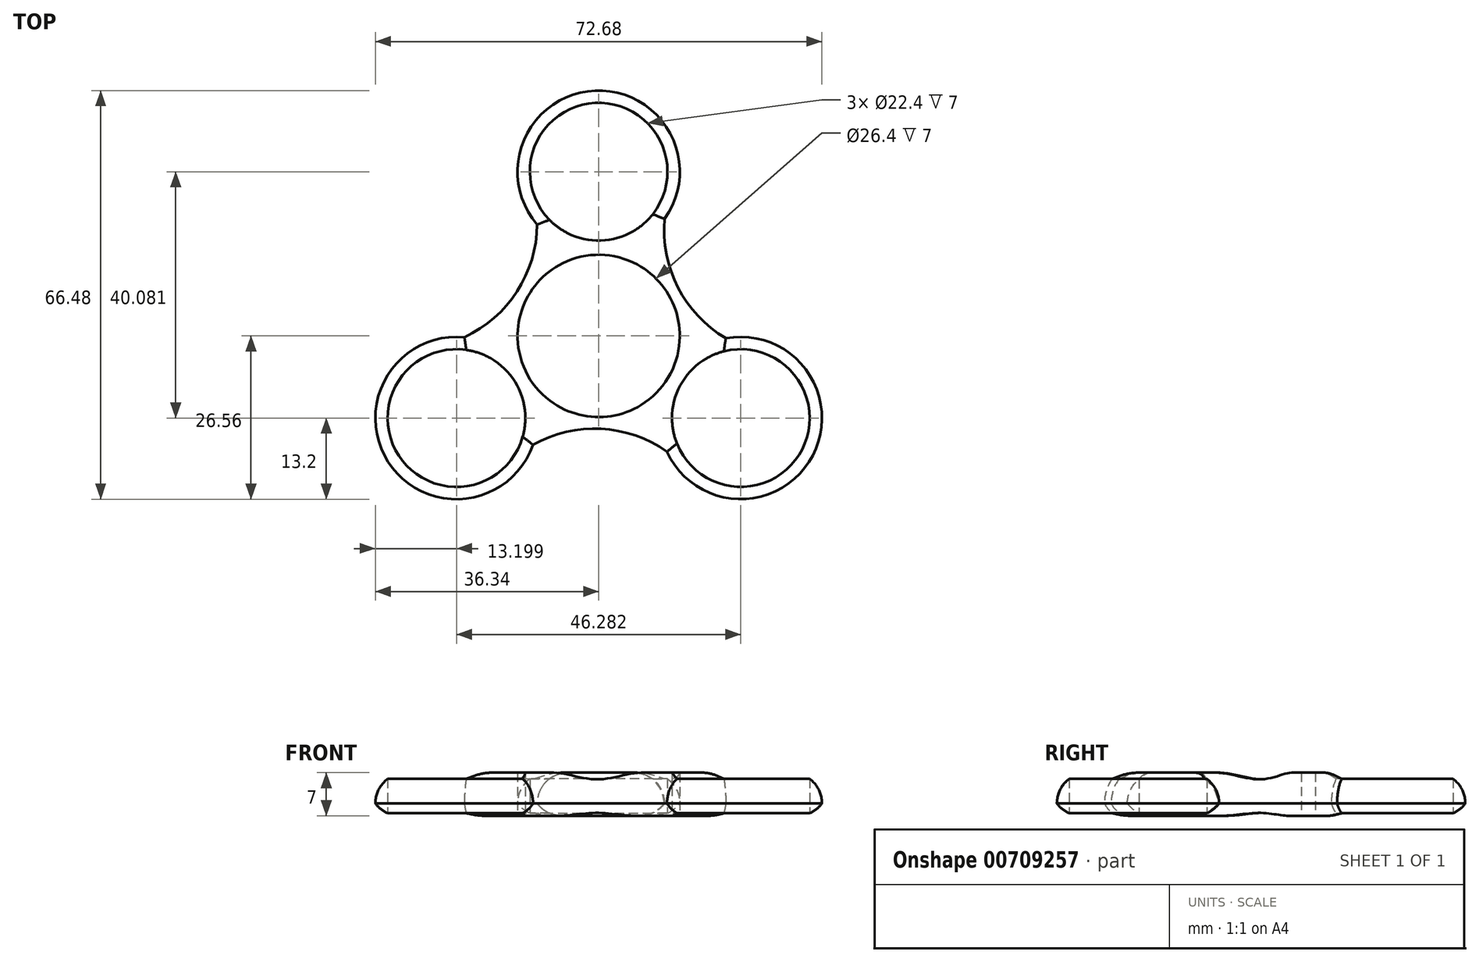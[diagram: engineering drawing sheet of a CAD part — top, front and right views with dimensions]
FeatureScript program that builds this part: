
annotation { "Feature Type Name" : "Feature", "Feature Type Description" : "" }
export const myFeature = defineFeature(function(context is Context, id is Id, definition is map)
    precondition{}
    {
        {
            var Q0;
            Q0=qCreatedBy(makeId("Top.planeOp"),FACE);
            var sketch = newSketch(context, id + "F0", { "sketchPlane" : qUnion([Q0])});
            skCircle(sketch, "E0", {"center": v(0, 0) * mm, "radius": 11.2 * mm});
            skCircle(sketch, "E1", {"center": v(0, 0) * mm, "radius": 13.2 * mm});
            skCircle(sketch, "E2", {"center": v(0, 26.72) * mm, "radius": 11.2 * mm});
            skArc(sketch, "E3", {"start": v(10.74, 19.04) * mm, "mid": v(-0.59, 39.9) * mm, "end": v(-10.01, 18.12) * mm});
            skArc(sketch, "E4.1.0", {"start": v(-21.86, -0.22) * mm, "mid": v(-34.27, -20.46) * mm, "end": v(-10.68, -17.73) * mm});
            skCircle(sketch, "E4.1.1", {"center": v(-23.14, -13.36) * mm, "radius": 11.2 * mm});
            skArc(sketch, "E4.2.0", {"start": v(11.12, -18.82) * mm, "mid": v(34.86, -19.44) * mm, "end": v(20.7, -0.39) * mm});
            skCircle(sketch, "E4.2.1", {"center": v(23.14, -13.36) * mm, "radius": 11.2 * mm});
            skArc(sketch, "E5", {"start": v(10.74, 19.04) * mm, "mid": v(12.9, 7.89) * mm, "end": v(20.7, -0.39) * mm});
            skArc(sketch, "E6.1.0", {"start": v(-21.86, -0.22) * mm, "mid": v(-13.28, 7.23) * mm, "end": v(-10.01, 18.12) * mm});
            skArc(sketch, "E6.2.0", {"start": v(11.12, -18.82) * mm, "mid": v(0.38, -15.12) * mm, "end": v(-10.68, -17.73) * mm});
            skSolve(sketch);
        }
        {
            var Q0;
            Q0=makeQuery(id+"F0.imprint","IMPRINT",FACE,{"disambiguationData":[TD([[makeQuery(id+"F0.imprint","IMPRINT",EDGE,{"derivedFrom":sQuery(id+"F0.wireOp",EDGE,"E1")}),-1.0]])]});
            extrude(context, id + "F1", {"entities" : qUnion([Q0]), "depth" : 7 * mm, "offsetDistance" : 25 * mm});
        }
        {
            var Q0;
            Q0=makeQuery(id+"F1.opExtrude","CAP_EDGE",EDGE,{"disambiguationData":[OSD([sQuery(id+"F0.wireOp",EDGE,"E3")])],"isStart":false});
            var Q1;
            Q1=makeQuery(id+"F1.opExtrude","CAP_EDGE",EDGE,{"disambiguationData":[OSD([sQuery(id+"F0.wireOp",EDGE,"E6.1.0")])],"isStart":false});
            var Q2;
            Q2=makeQuery(id+"F1.opExtrude","CAP_EDGE",EDGE,{"disambiguationData":[OSD([sQuery(id+"F0.wireOp",EDGE,"E4.1.0")])],"isStart":false});
            var Q3;
            Q3=makeQuery(id+"F1.opExtrude","CAP_EDGE",EDGE,{"disambiguationData":[OSD([sQuery(id+"F0.wireOp",EDGE,"E6.2.0")])],"isStart":false});
            var Q4;
            Q4=makeQuery(id+"F1.opExtrude","CAP_EDGE",EDGE,{"disambiguationData":[OSD([sQuery(id+"F0.wireOp",EDGE,"E4.2.0")])],"isStart":false});
            var Q5;
            Q5=makeQuery(id+"F1.opExtrude","CAP_EDGE",EDGE,{"disambiguationData":[OSD([sQuery(id+"F0.wireOp",EDGE,"E5")])],"isStart":false});
            fillet(context, id + "F2", {"entities" : qUnion([Q0, Q1, Q2, Q3, Q4, Q5]), "radius" : 5 * mm, "tangentPropagation" : true, "allowEdgeOverflow" : false});
        }
        {
            var Q0;
            Q0=makeQuery(id+"F1.opExtrude","CAP_EDGE",EDGE,{"disambiguationData":[OSD([sQuery(id+"F0.wireOp",EDGE,"E6.1.0")])],"isStart":true});
            var Q1;
            Q1=makeQuery(id+"F1.opExtrude","CAP_EDGE",EDGE,{"disambiguationData":[OSD([sQuery(id+"F0.wireOp",EDGE,"E5")])],"isStart":true});
            var Q2;
            Q2=makeQuery(id+"F1.opExtrude","CAP_EDGE",EDGE,{"disambiguationData":[OSD([sQuery(id+"F0.wireOp",EDGE,"E6.2.0")])],"isStart":true});
            fillet(context, id + "F3", {"entities" : qUnion([Q0, Q1, Q2]), "radius" : 5 * mm, "tangentPropagation" : true, "allowEdgeOverflow" : false});
        }
        {
            var Q0;
            Q0=makeQuery(id+"F1.opExtrude","CAP_EDGE",EDGE,{"disambiguationData":[OSD([sQuery(id+"F0.wireOp",EDGE,"E3")])],"isStart":true});
            var Q1;
            Q1=makeQuery(id+"F1.opExtrude","CAP_EDGE",EDGE,{"disambiguationData":[OSD([sQuery(id+"F0.wireOp",EDGE,"E4.2.0")])],"isStart":true});
            var Q2;
            Q2=makeQuery(id+"F1.opExtrude","CAP_EDGE",EDGE,{"disambiguationData":[OSD([sQuery(id+"F0.wireOp",EDGE,"E4.1.0")])],"isStart":true});
            fillet(context, id + "F4", {"entities" : qUnion([Q0, Q1, Q2]), "radius" : 5 * mm, "tangentPropagation" : true, "allowEdgeOverflow" : false});
        }
    });
